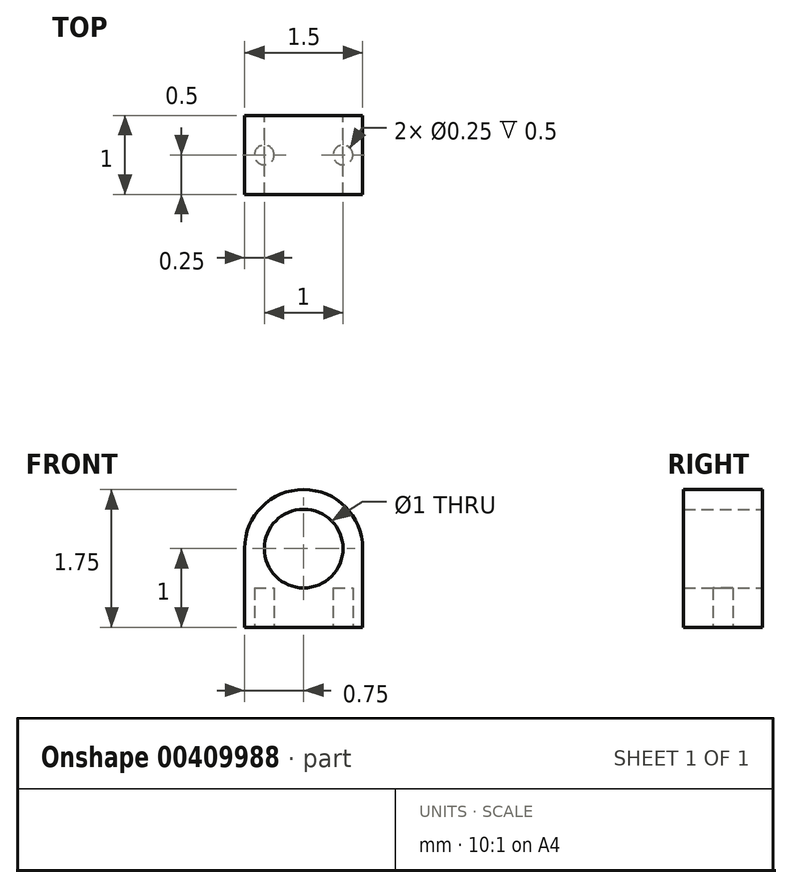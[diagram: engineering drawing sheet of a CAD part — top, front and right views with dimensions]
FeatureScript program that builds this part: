
annotation { "Feature Type Name" : "Feature", "Feature Type Description" : "" }
export const myFeature = defineFeature(function(context is Context, id is Id, definition is map)
    precondition{}
    {
        {
            var Q0;
            Q0=qCreatedBy(makeId("Front.planeOp"),FACE);
            var sketch = newSketch(context, id + "F0", { "sketchPlane" : qUnion([Q0])});
            skLineSegment(sketch, "E0.top", {"start": v(-0.75, 0) * mm, "end": v(0.75, 0) * mm});
            skLineSegment(sketch, "E0.left", {"start": v(-0.75, 1) * mm, "end": v(-0.75, 0) * mm});
            skLineSegment(sketch, "E0.right", {"start": v(0.75, 1) * mm, "end": v(0.75, 0) * mm});
            skArc(sketch, "E1", {"start": v(0.75, 1) * mm, "mid": v(0, 1.75) * mm, "end": v(-0.75, 1) * mm});
            skCircle(sketch, "E2", {"center": v(0, 1) * mm, "radius": 0.5 * mm});
            skSolve(sketch);
        }
        {
            var Q0;
            Q0=makeQuery(id+"F0.imprint","IMPRINT",FACE,{"disambiguationData":[TD([[makeQuery(id+"F0.imprint","IMPRINT",EDGE,{"derivedFrom":sQuery(id+"F0.wireOp",EDGE,"E0.top")}),1.0]])]});
            extrude(context, id + "F1", {"entities" : qUnion([Q0]), "depth" : 1 * mm});
        }
        {
            var Q0;
            Q0=makeQuery(id+"F1.opExtrude","SWEPT_FACE",FACE,{"disambiguationData":[OSD([sQuery(id+"F0.wireOp",EDGE,"E0.top")])]});
            var sketch = newSketch(context, id + "F2", { "sketchPlane" : qUnion([Q0])});
            skCircle(sketch, "E3", {"center": v(-0.5, 0.5) * mm, "radius": 0.12 * mm});
            skSolve(sketch);
        }
        {
            var Q0;
            Q0=makeQuery(id+"F2.imprint","IMPRINT",FACE,{"disambiguationData":[TD([[makeQuery(id+"F2.imprint","IMPRINT",EDGE,{"derivedFrom":sQuery(id+"F2.wireOp",EDGE,"E3")}),1.0]])]});
            extrude(context, id + "F3", {"entities" : qUnion([Q0]), "operationType" : NewBodyOperationType.REMOVE, "oppositeDirection" : true, "depth" : 0.5 * mm});
        }
        {
            var Q0;
            Q0=makeQuery(id+"F1.opExtrude","SWEPT_FACE",FACE,{"disambiguationData":[OSD([sQuery(id+"F0.wireOp",EDGE,"E0.top")])]});
            var sketch = newSketch(context, id + "F4", { "sketchPlane" : qUnion([Q0])});
            skCircle(sketch, "E4", {"center": v(0.5, 0.5) * mm, "radius": 0.13 * mm});
            skSolve(sketch);
        }
        {
            var Q0;
            Q0=makeQuery(id+"F4.imprint","IMPRINT",FACE,{"disambiguationData":[TD([[makeQuery(id+"F4.imprint","IMPRINT",EDGE,{"derivedFrom":sQuery(id+"F4.wireOp",EDGE,"E4")}),1.0]])]});
            extrude(context, id + "F5", {"entities" : qUnion([Q0]), "operationType" : NewBodyOperationType.REMOVE, "oppositeDirection" : true, "depth" : 0.5 * mm});
        }
    });
